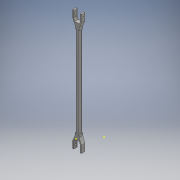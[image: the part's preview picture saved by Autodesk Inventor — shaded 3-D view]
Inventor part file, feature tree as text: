
AUTODESK INVENTOR PART (.ipt)
format: ipt  version: 2016 (Build 200138000, 138)  size: 198,656 bytes
history: native  units: mm
features: sketch x9, extrude x7
ambient origin geometry x8: Origin, YZ Plane, XZ Plane, XY Plane, X Axis, Y Axis, Z Axis, Center Point
bodies: Solid1 (feature_tree)
feature tree (16):
  extrude  "Extrusion1"  Depth=164.0mm TaperAngle=0.0deg
  extrude  "Extrusion2"  Depth=2.0mm
  sketch  "Sketch3"  dims[d16=27.824719mm d17=11.0mm]
  extrude  "Extrusion3"  Depth=11.0mm
  extrude  "Extrusion4"  Depth=6.5mm TaperAngle=0.0deg
  extrude  "Extrusion5"  Depth=6.5mm
  extrude  "Extrusion6"  Depth=6.5mm TaperAngle=0.0deg
  sketch  "Sketch9"  dims[d34=2.0mm d35=2.0mm d36=11.0mm d37=12.0mm d38=2.0mm d39=2.0mm]
  extrude  "Extrusion7"  Depth=2.0mm
  sketch  "Sketch1"  dims[d0=7.5mm d1=164.0mm d2=0.0mm]
  sketch  "Sketch2"  dims[d12=2.0mm d13=2.0mm]
  sketch  "Sketch5"  dims[d21=12.0mm d22=6.5mm d23=0.0mm]
  sketch  "Sketch6"  dims[d25=6.5mm d26=0.0mm d27=6.0mm]
  sketch  "Sketch7"  dims[d28=3.0mm d29=6.5mm d30=0.0mm]
  sketch  "Sketch8"  dims[d31=2.0mm d32=2.0mm]
  sketch  "Sketch10"  dims[d40=6.5mm d41=0.0mm d42=6.5mm d43=0.0mm d44=6.0mm d45=3.0mm d46=10.0mm d47=0.0mm]
